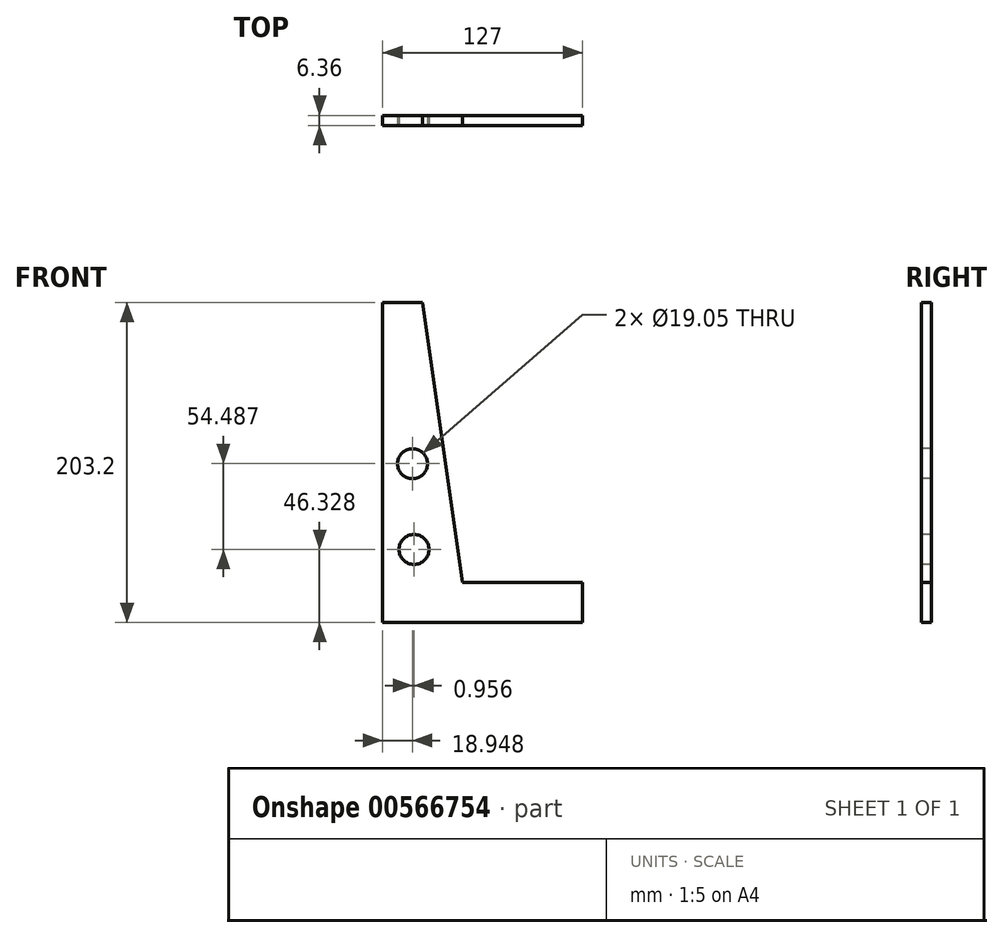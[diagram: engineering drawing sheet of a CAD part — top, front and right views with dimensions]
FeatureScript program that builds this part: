
annotation { "Feature Type Name" : "Feature", "Feature Type Description" : "" }
export const myFeature = defineFeature(function(context is Context, id is Id, definition is map)
    precondition{}
    {
        {
            var Q0;
            Q0=qCreatedBy(makeId("Front.planeOp"),FACE);
            var sketch = newSketch(context, id + "F0", { "sketchPlane" : qUnion([Q0])});
            skLineSegment(sketch, "E0", {"start": v(0, 177.8) * mm, "end": v(0, -25.4) * mm});
            skLineSegment(sketch, "E1", {"start": v(0, -25.4) * mm, "end": v(127, -25.4) * mm});
            skLineSegment(sketch, "E2", {"start": v(127, -25.4) * mm, "end": v(127, 0) * mm});
            skLineSegment(sketch, "E3", {"start": v(127, 0) * mm, "end": v(50.8, 0) * mm});
            skLineSegment(sketch, "E4", {"start": v(50.8, 0) * mm, "end": v(25.4, 177.8) * mm});
            skLineSegment(sketch, "E5", {"start": v(25.4, 177.8) * mm, "end": v(0, 177.8) * mm});
            skSolve(sketch);
        }
        {
            var Q0;
            Q0 = qSketchRegion(id + "F0", true);
            var Q1;
            Q1=makeQuery(id+"F0.imprint","IMPRINT",FACE,{"disambiguationData":[TD([[makeQuery(id+"F0.imprint","IMPRINT",EDGE,{"derivedFrom":sQuery(id+"F0.wireOp",EDGE,"E0")}),1.0]])]});
            extrude(context, id + "F1", {"entities" : qUnion([Q0, Q1]), "endBound" : BoundingType.SYMMETRIC, "depth" : 6.35 * mm, "offsetDistance" : 25.4 * mm});
        }
        {
            var Q0;
            Q0=makeQuery(id+"F1.opExtrude","CAP_FACE",FACE,{"disambiguationData":[OSD([sQuery(id+"F0.wireOp",EDGE,"E0"),sQuery(id+"F0.wireOp",EDGE,"E1"),sQuery(id+"F0.wireOp",EDGE,"E2"),sQuery(id+"F0.wireOp",EDGE,"E3"),sQuery(id+"F0.wireOp",EDGE,"E4"),sQuery(id+"F0.wireOp",EDGE,"E5")])],"isStart":false});
            var sketch = newSketch(context, id + "F2", { "sketchPlane" : qUnion([Q0])});
            skPoint(sketch, "E6", {"position": v(18.95, 75.41) * mm});
            skPoint(sketch, "E7", {"position": v(19.9, 20.93) * mm});
            skSolve(sketch);
        }
        {
            var Q0;
            Q0=sQuery(id+"F2.wireOp",VERTEX,"E6");
            var Q1;
            Q1=sQuery(id+"F2.wireOp",VERTEX,"E7");
            var Q2;
            Q2=makeQuery(id+"F1.opExtrude","SWEPT_BODY",BODY,{"disambiguationData":[OSD([sQuery(id+"F0.wireOp",EDGE,"E0"),sQuery(id+"F0.wireOp",EDGE,"E1"),sQuery(id+"F0.wireOp",EDGE,"E2"),sQuery(id+"F0.wireOp",EDGE,"E3"),sQuery(id+"F0.wireOp",EDGE,"E4"),sQuery(id+"F0.wireOp",EDGE,"E5")])]});
            hole(context, id + "F3", {"style" : HoleStyle.SIMPLE, "endStyle" : HoleEndStyle.THROUGH, "holeDiameter" : 19.05 * mm, "majorDiameter" : 6.35 * mm, "isTappedThrough" : true, "tappedDepth" : 12.7 * mm, "tapClearance" : 3, "locations" : qUnion([Q0, Q1]), "scope" : qUnion([Q2])});
        }
    });
